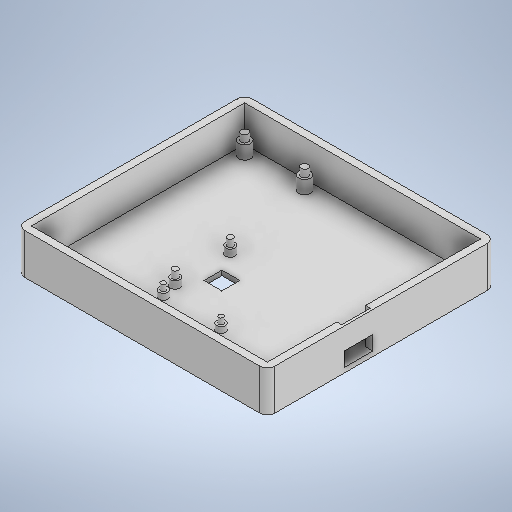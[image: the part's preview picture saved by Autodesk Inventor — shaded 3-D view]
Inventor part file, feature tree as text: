
AUTODESK INVENTOR PART (.ipt)
format: ipt  version: 2025.2 (Build 292293000, 293)  size: 406,016 bytes
history: native  units: in
note: dims shown in document units (in); Inventor stores cm internally (conversion verified against a paired STEP export)
features: extrude x11, sketch x3, fillet x1, projected_geometry x1
ambient origin geometry x8: Origin, YZ Plane, XZ Plane, XY Plane, X Axis, Y Axis, Z Axis, Center Point
bodies: Solid1 (feature_tree)
feature tree (16):
  sketch  "Sketch1"  dims[d0=0.0984in d1=2.2835in]
  extrude  "Extrusion1"  Depth=2.2835in
  extrude  "Extrusion2"  Depth=0.0984in
  extrude  "Extrusion3"  TaperAngle=270.0deg  [1 undecoded]
  extrude  "Extrusion4"  TaperAngle=90.0deg  [1 undecoded]
  extrude  "Extrusion5"  Depth=0.0984in
  extrude  "Extrusion6"  Depth=0.0984in
  extrude  "Extrusion7"  Depth=0.125in
  extrude  "Extrusion8"  Depth=0.125in
  extrude  "Extrusion9"  Depth=0.125in
  extrude  "Extrusion10"  Depth=0.125in
  extrude  "Extrusion11"  Depth=0.125in
  fillet  "Fillet1"  Radius=0.1575in
  sketch  "Sketch2"  dims[d2=180.0deg d3=0.0984in]
  sketch  "Sketch3"  dims[d4=0.9055in d5=270.0deg d6=90.0deg d7=0.0984in d8=0.0984in d9=2.5591in d10=1.1811in d11=0.1575in d12=0.1575in d13=0.1575in d14=0.1575in d15=0.0197in d16=1.25in d17=0.75in d18=0.2in d19=0.1in d20=0.08in d21=0.2in d22=0.1in d23=0.1in d24=0.1in d25=0.1in d26=0.1in d27=0.08in d28=0.08in d29=0.08in d30=0.15in d31=0.15in d32=0.15in d33=0.15in d34=0.0197in d35=2.4469in d36=1.4961in d37=0.0197in d38=1.2598in d39=3.4252in d40=0.9843in d41=3.1496in d42=0.1181in d43=0.1181in d44=0.1181in d45=0.1181in d46=0.1969in d47=0.1969in d48=0.1969in d49=0.1969in d50=0.0197in d51=0.0197in d52=0.0197in d53=0.0197in d54=0.0787in d55=0.0in d56=0.1181in d57=0.5906in d58=0.0in d59=0.4528in d60=0.2953in d61=0.2953in d62=0.3937in d63=0.0in d64=0.2165in d65=0.0in d66=0.3346in d67=0.0in d68=0.1181in d69=0.0in d70=0.2362in d71=0.0in d72=0.0984in d73=0.0in d74=0.1969in d75=0.0in d76=0.4724in d77=180.0deg d78=0.5906in d79=0.0in d80=0.0787in d81=1.0in d82=0.0in d83=0.125in]
  projected_geometry  "Projected Loop1"
note: 2 required parameter values undecoded (feature->parameter linkage not recoverable at this tier; creation-order binding heuristic only, values carry confidence <= 0.55)
